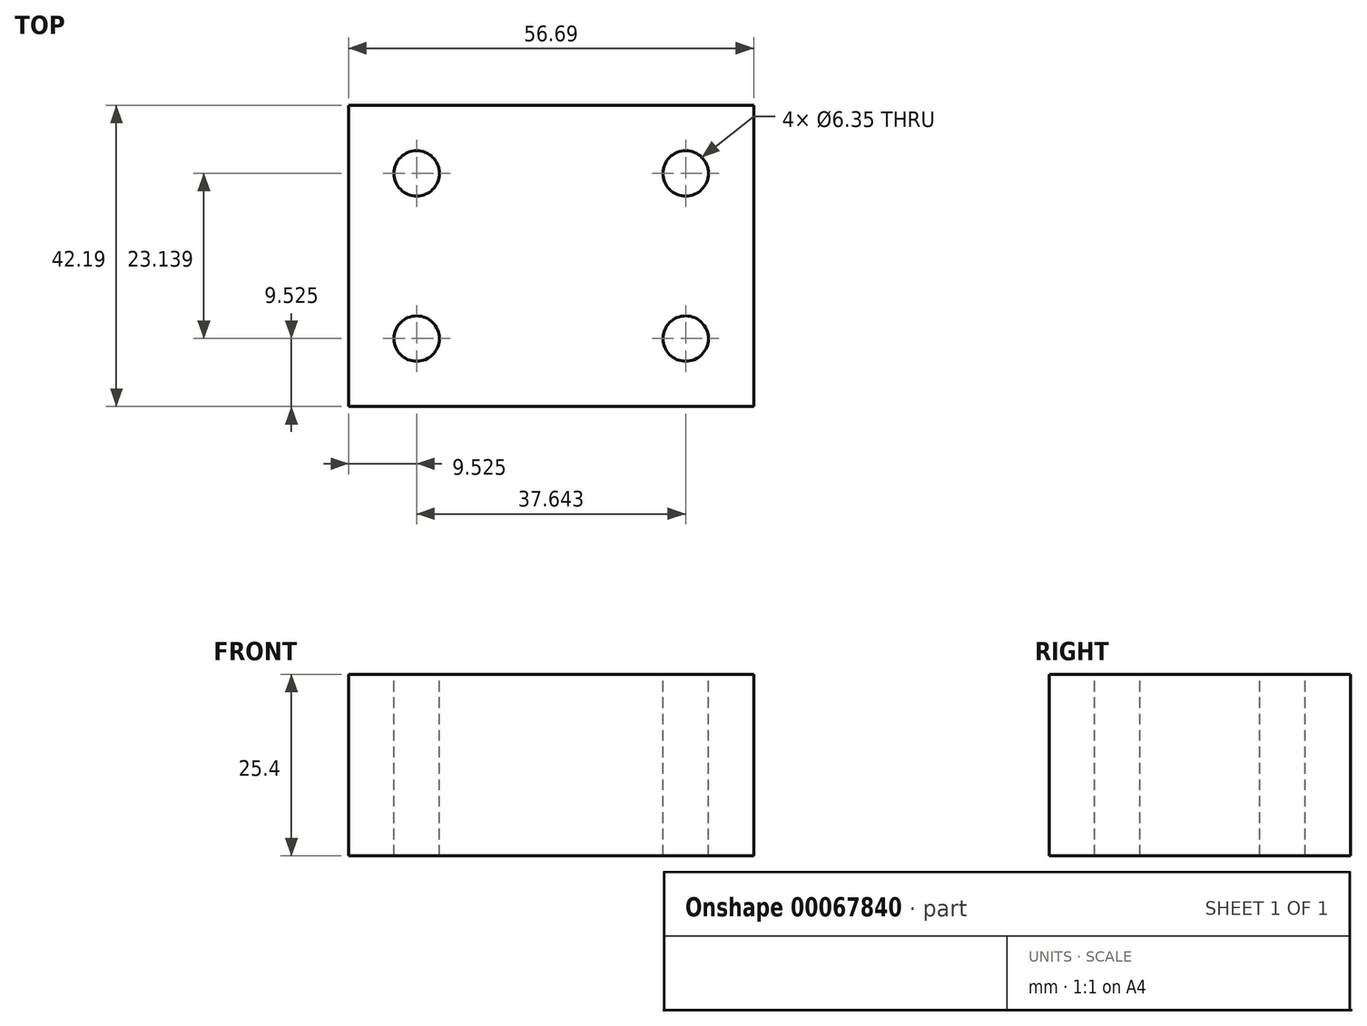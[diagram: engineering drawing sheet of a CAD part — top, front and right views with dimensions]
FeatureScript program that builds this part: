
annotation { "Feature Type Name" : "Feature", "Feature Type Description" : "" }
export const myFeature = defineFeature(function(context is Context, id is Id, definition is map)
    precondition{}
    {
        {
            var Q0;
            Q0=qCreatedBy(makeId("Top.planeOp"),FACE);
            var sketch = newSketch(context, id + "F0", { "sketchPlane" : qUnion([Q0])});
            skLineSegment(sketch, "E0.bottom", {"start": v(0, 0) * mm, "end": v(56.7, 0) * mm});
            skLineSegment(sketch, "E0.top", {"start": v(0, 42.19) * mm, "end": v(56.7, 42.19) * mm});
            skLineSegment(sketch, "E0.left", {"start": v(0, 0) * mm, "end": v(0, 42.19) * mm});
            skLineSegment(sketch, "E0.right", {"start": v(56.7, 0) * mm, "end": v(56.7, 42.19) * mm});
            skSolve(sketch);
        }
        {
            var Q0;
            Q0=makeQuery(id+"F0.imprint","IMPRINT",FACE,{"disambiguationData":[TD([[makeQuery(id+"F0.imprint","IMPRINT",EDGE,{"derivedFrom":sQuery(id+"F0.wireOp",EDGE,"E0.bottom")}),1.0]])]});
            extrude(context, id + "F1", {"entities" : qUnion([Q0]), "depth" : 25.4 * mm});
        }
        {
            var Q0;
            Q0=makeQuery(id+"F1.opExtrude","CAP_FACE",FACE,{"disambiguationData":[OSD([sQuery(id+"F0.wireOp",EDGE,"E0.bottom"),sQuery(id+"F0.wireOp",EDGE,"E0.top"),sQuery(id+"F0.wireOp",EDGE,"E0.left"),sQuery(id+"F0.wireOp",EDGE,"E0.right")])],"isStart":false});
            var sketch = newSketch(context, id + "F2", { "sketchPlane" : qUnion([Q0])});
            skPoint(sketch, "E1", {"position": v(9.52, 32.66) * mm});
            skPoint(sketch, "E2", {"position": v(47.17, 32.66) * mm});
            skPoint(sketch, "E3", {"position": v(47.17, 9.53) * mm});
            skPoint(sketch, "E4", {"position": v(9.53, 9.53) * mm});
            skSolve(sketch);
        }
        {
            var Q0;
            Q0=sQuery(id+"F2.wireOp",VERTEX,"E4");
            var Q1;
            Q1=sQuery(id+"F2.wireOp",VERTEX,"E1");
            var Q2;
            Q2=sQuery(id+"F2.wireOp",VERTEX,"E2");
            var Q3;
            Q3=sQuery(id+"F2.wireOp",VERTEX,"E3");
            var Q4;
            Q4=makeQuery(id+"F1.opExtrude","SWEPT_BODY",BODY,{"disambiguationData":[OSD([sQuery(id+"F0.wireOp",EDGE,"E0.bottom"),sQuery(id+"F0.wireOp",EDGE,"E0.top"),sQuery(id+"F0.wireOp",EDGE,"E0.left"),sQuery(id+"F0.wireOp",EDGE,"E0.right")])]});
            hole(context, id + "F3", {"style" : HoleStyle.SIMPLE, "holeDiameter" : 6.35 * mm, "endStyle" : HoleEndStyle.THROUGH, "locations" : qUnion([Q0, Q1, Q2, Q3]), "scope" : qUnion([Q4])});
        }
    });
